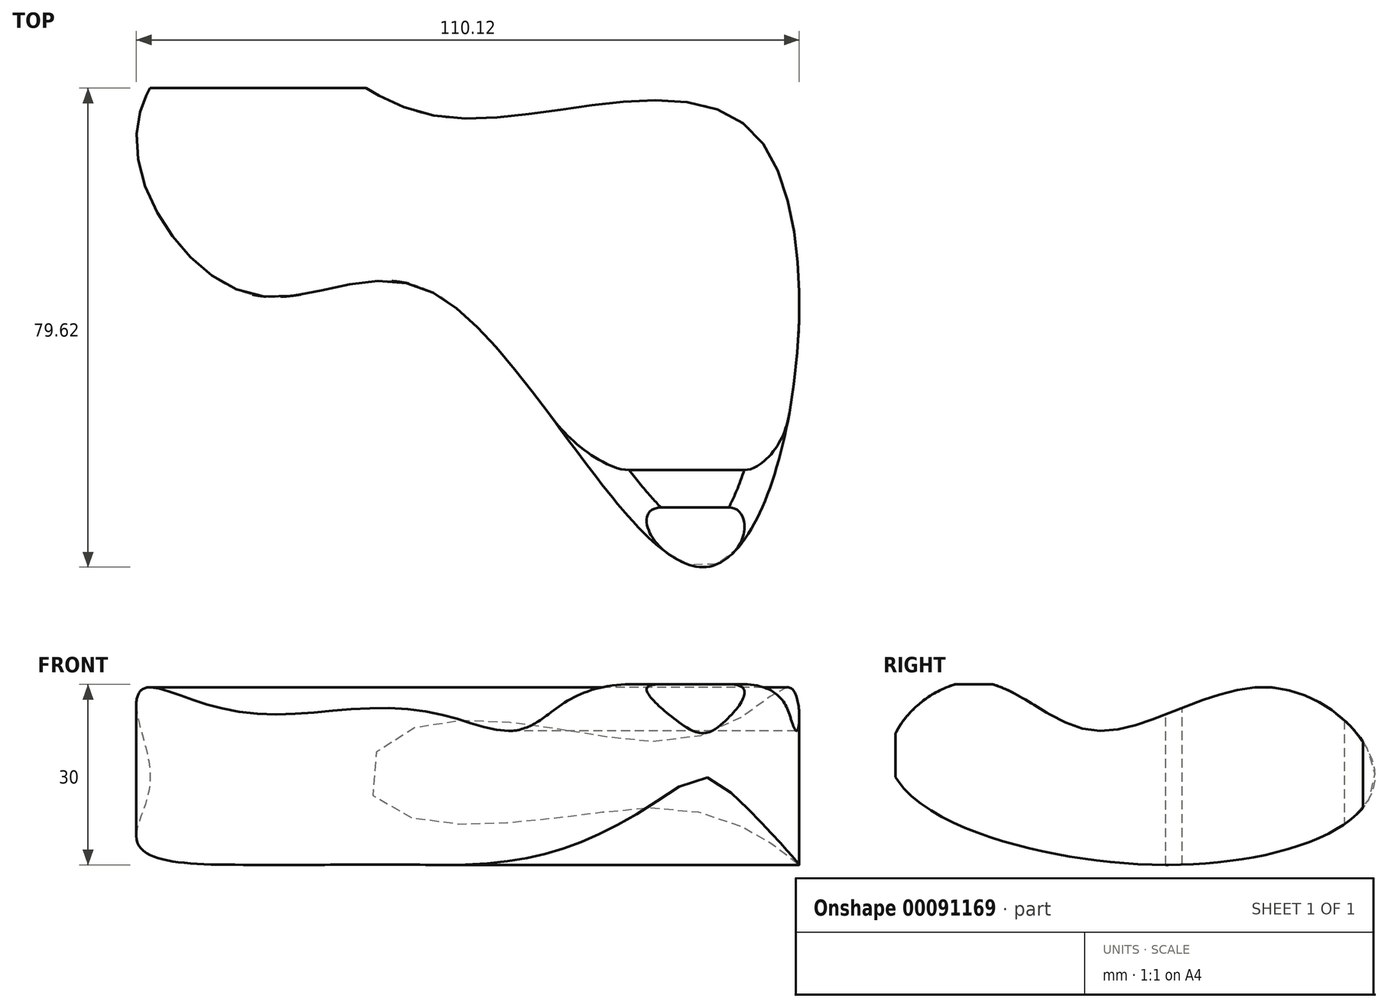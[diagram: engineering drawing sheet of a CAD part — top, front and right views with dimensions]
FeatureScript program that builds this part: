
annotation { "Feature Type Name" : "Feature", "Feature Type Description" : "" }
export const myFeature = defineFeature(function(context is Context, id is Id, definition is map)
    precondition{}
    {
        {
            var Q0;
            Q0=qCreatedBy(makeId("Top.planeOp"),FACE);
            var sketch = newSketch(context, id + "F0", { "sketchPlane" : qUnion([Q0])});
            skFitSpline(sketch, "E0", {"points": [v(0, 0) * mm, v(45.78, -45.1) * mm, v(53.78, 25.63) * mm, v(0, 29.64) * mm, v(-30.03, 44.33) * mm, v(-49.73, 28.03) * mm, v(-30.65, 0) * mm, v(0, 0) * mm]});
            skSolve(sketch);
        }
        {
            var Q0;
            Q0=makeQuery(id+"F0.imprint","IMPRINT",FACE,{"disambiguationData":[TD([[makeQuery(id+"F0.imprint","IMPRINT",EDGE,{"derivedFrom":sQuery(id+"F0.wireOp",EDGE,"E0")}),1.0]])]});
            extrude(context, id + "F1", {"entities" : qUnion([Q0]), "depth" : 30 * mm});
        }
        {
            var Q0;
            Q0=qCreatedBy(makeId("Right.planeOp"),FACE);
            var sketch = newSketch(context, id + "F2", { "sketchPlane" : qUnion([Q0])});
            skFitSpline(sketch, "E1", {"points": [v(-46.19, 17.1) * mm, v(-32.58, 30.47) * mm, v(-12.4, 22.32) * mm, v(17.46, 29.46) * mm, v(34.28, 13.92) * mm, v(0, 0) * mm, v(-46.19, 17.1) * mm]});
            skSolve(sketch);
        }
        {
            var Q0;
            Q0 = qSketchRegion(id + "F2", true);
            extrude(context, id + "F3", {"entities" : qUnion([Q0]), "operationType" : NewBodyOperationType.INTERSECT, "depth" : 68 * mm, "hasSecondDirection" : true, "secondDirectionOppositeDirection" : true, "secondDirectionDepth" : 56 * mm});
        }
        {
            var Q0;
            Q0=makeQuery(id+"F3.boolean.opBoolean","INTERSECT",EDGE,{"disambiguationData":[OD(2.0)],"derivedFrom":[makeQuery(id+"F1.opExtrude","SWEPT_FACE",FACE,{"disambiguationData":[OSD([sQuery(id+"F0.wireOp",EDGE,"E0")])]}),makeQuery(id+"F3.boolean.toolComplement.opBoolean","COPY",FACE,{"derivedFrom":makeQuery(id+"F3.opExtrude","SWEPT_FACE",FACE,{"disambiguationData":[OSD([sQuery(id+"F2.wireOp",EDGE,"E1")])]})})]});
            var Q1;
            Q1=makeQuery(id+"F3.boolean.opBoolean","SPLIT",EDGE,{"disambiguationData":[OD(0.0)],"derivedFrom":makeQuery(id+"F1.opExtrude","CAP_EDGE",EDGE,{"disambiguationData":[OSD([sQuery(id+"F0.wireOp",EDGE,"E0")])],"isStart":false})});
            var Q2;
            Q2=makeQuery(id+"F3.boolean.opBoolean","INTERSECT",EDGE,{"disambiguationData":[OD(0.0)],"derivedFrom":[makeQuery(id+"F1.opExtrude","SWEPT_FACE",FACE,{"disambiguationData":[OSD([sQuery(id+"F0.wireOp",EDGE,"E0")])]}),makeQuery(id+"F3.boolean.toolComplement.opBoolean","COPY",FACE,{"derivedFrom":makeQuery(id+"F3.opExtrude","SWEPT_FACE",FACE,{"disambiguationData":[OSD([sQuery(id+"F2.wireOp",EDGE,"E1")])]})})]});
            var Q3;
            Q3=makeQuery(id+"F3.boolean.opBoolean","INTERSECT",EDGE,{"disambiguationData":[OD(3.0)],"derivedFrom":[makeQuery(id+"F1.opExtrude","SWEPT_FACE",FACE,{"disambiguationData":[OSD([sQuery(id+"F0.wireOp",EDGE,"E0")])]}),makeQuery(id+"F3.boolean.toolComplement.opBoolean","COPY",FACE,{"derivedFrom":makeQuery(id+"F3.opExtrude","SWEPT_FACE",FACE,{"disambiguationData":[OSD([sQuery(id+"F2.wireOp",EDGE,"E1")])]})})]});
            var Q4;
            Q4=makeQuery(id+"F3.boolean.opBoolean","INTERSECT",EDGE,{"disambiguationData":[OD(1.0)],"derivedFrom":[makeQuery(id+"F1.opExtrude","SWEPT_FACE",FACE,{"disambiguationData":[OSD([sQuery(id+"F0.wireOp",EDGE,"E0")])]}),makeQuery(id+"F3.boolean.toolComplement.opBoolean","COPY",FACE,{"derivedFrom":makeQuery(id+"F3.opExtrude","SWEPT_FACE",FACE,{"disambiguationData":[OSD([sQuery(id+"F2.wireOp",EDGE,"E1")])]})})]});
            var Q5;
            Q5=makeQuery(id+"F3.boolean.opBoolean","SPLIT",EDGE,{"disambiguationData":[OD(1.0)],"derivedFrom":makeQuery(id+"F1.opExtrude","CAP_EDGE",EDGE,{"disambiguationData":[OSD([sQuery(id+"F0.wireOp",EDGE,"E0")])],"isStart":false})});
            fillet(context, id + "F4", {"entities" : qUnion([Q0, Q1, Q2, Q3, Q4, Q5]), "radius" : 5 * mm, "tangentPropagation" : true, "rho" : 0.5, "crossSection" : FilletCrossSection.CONIC, "allowEdgeOverflow" : false});
        }
    });
